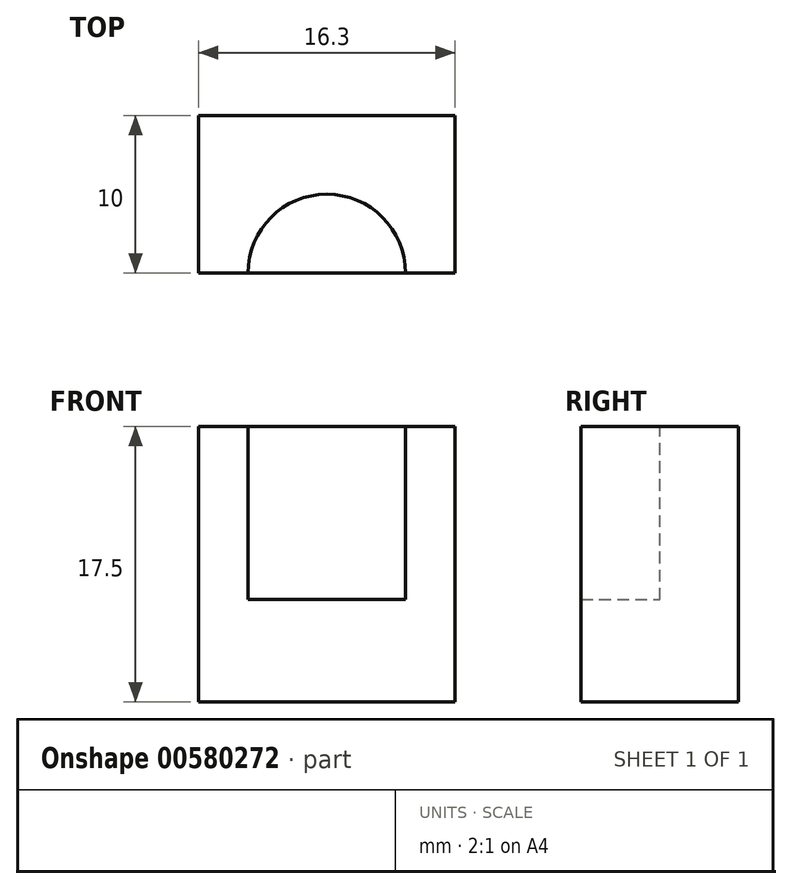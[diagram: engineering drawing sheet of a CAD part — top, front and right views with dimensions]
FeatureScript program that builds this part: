
annotation { "Feature Type Name" : "Feature", "Feature Type Description" : "" }
export const myFeature = defineFeature(function(context is Context, id is Id, definition is map)
    precondition{}
    {
        {
            var Q0;
            Q0=qCreatedBy(makeId("Top.planeOp"),FACE);
            var sketch = newSketch(context, id + "F0", { "sketchPlane" : qUnion([Q0])});
            skLineSegment(sketch, "E0.bottom", {"start": v(8.15, -5) * mm, "end": v(-8.15, -5) * mm});
            skLineSegment(sketch, "E0.top", {"start": v(8.15, 5) * mm, "end": v(-8.15, 5) * mm});
            skLineSegment(sketch, "E0.left", {"start": v(8.15, -5) * mm, "end": v(8.15, 5) * mm});
            skLineSegment(sketch, "E0.right", {"start": v(-8.15, -5) * mm, "end": v(-8.15, 5) * mm});
            skPoint(sketch, "E0.middle", {"position": v(0, 0) * mm});
            skSolve(sketch);
        }
        {
            var Q0;
            Q0=makeQuery(id+"F0.imprint","IMPRINT",FACE,{"disambiguationData":[TD([[makeQuery(id+"F0.imprint","IMPRINT",EDGE,{"derivedFrom":sQuery(id+"F0.wireOp",EDGE,"E0.bottom")}),-1.0]])]});
            extrude(context, id + "F1", {"entities" : qUnion([Q0]), "depth" : 17.5 * mm, "offsetDistance" : 25 * mm});
        }
        {
            var Q0;
            Q0=makeQuery(id+"F1.opExtrude","CAP_FACE",FACE,{"disambiguationData":[OSD([sQuery(id+"F0.wireOp",EDGE,"E0.bottom"),sQuery(id+"F0.wireOp",EDGE,"E0.top"),sQuery(id+"F0.wireOp",EDGE,"E0.left"),sQuery(id+"F0.wireOp",EDGE,"E0.right")])],"isStart":false});
            var sketch = newSketch(context, id + "F2", { "sketchPlane" : qUnion([Q0])});
            skLineSegment(sketch, "E1", {"start": v(0, 10.26) * mm, "end": v(0, -10.98) * mm, "construction": true});
            skLineSegment(sketch, "E2", {"start": v(-14.23, -5) * mm, "end": v(15.83, -5) * mm, "construction": true});
            skCircle(sketch, "E3", {"center": v(0, -5) * mm, "radius": 5 * mm});
            skLineSegment(sketch, "E4", {"start": v(-12.3, 0) * mm, "end": v(11.98, 0) * mm, "construction": true});
            skSolve(sketch);
        }
        {
            var Q0;
            {var subQ0=sQuery(id+"F2.wireOp",EDGE,"E3");var subQ1=makeQuery(id+"F1.opExtrude","CAP_EDGE",EDGE,{"disambiguationData":[OSD([sQuery(id+"F0.wireOp",EDGE,"E0.bottom")])],"isStart":false});var subQ2=makeQuery(id+"F2.imprint","INTERSECT",VERTEX,{"disambiguationData":[OD(0.0)],"derivedFrom":[subQ1,subQ0]});Q0=makeQuery(id+"F2.imprint","IMPRINT",FACE,{"disambiguationData":[TD([[makeQuery(id+"F2.imprint","IMPRINT",EDGE,{"disambiguationData":[TD([[subQ2,-1.0]])],"derivedFrom":subQ0}),1.0]])]});}
            extrude(context, id + "F3", {"entities" : qUnion([Q0]), "operationType" : NewBodyOperationType.REMOVE, "oppositeDirection" : true, "depth" : 11 * mm, "offsetDistance" : 25 * mm});
        }
    });
